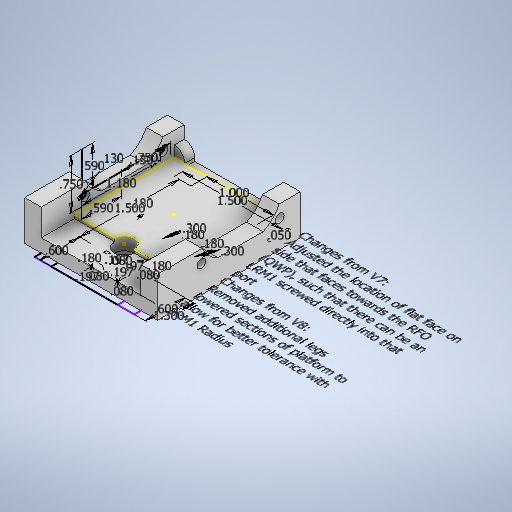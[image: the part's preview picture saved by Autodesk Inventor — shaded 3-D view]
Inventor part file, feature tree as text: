
AUTODESK INVENTOR PART (.ipt)
format: ipt  version: 2025.2 (Build 292293000, 293)  size: 535,040 bytes
history: native  units: in
note: dims shown in document units (in); Inventor stores cm internally (conversion verified against a paired STEP export)
features: sketch x15, extrude x13, thicken_offset x6, move_body x5, direct_edit x4, projected_geometry x2
ambient origin geometry x8: Origin, YZ Plane, XZ Plane, XY Plane, X Axis, Y Axis, Z Axis, Center Point
bodies: Solid1 (feature_tree)
feature tree (45):
  sketch  "Sketch1"  dims[d0=1.5in d1=1.0in]
  extrude  "Extrusion1"  Depth=1.5in
  extrude  "Extrusion2"  Depth=0.6in
  extrude  "Extrusion3"  Depth=1.5in
  extrude  "Extrusion4"  Depth=0.18in
  sketch  "Sketch3"  dims[d4=1.5in d5=0.18in]
  extrude  "Extrusion5"  Depth=0.05in
  sketch  "Sketch4"  dims[d6=0.18in d7=0.18in]
  extrude  "Extrusion6"  Depth=0.6in
  extrude  "Extrusion7"  Depth=0.3in
  extrude  "Extrusion8"  Depth=0.2in TaperAngle=0.0deg
  extrude  "Extrusion9"  Depth=0.2in TaperAngle=0.0deg
  thicken_offset  "Thicken1"
  thicken_offset  "Thicken2"
  thicken_offset  "Thicken3"
  thicken_offset  "Thicken4"
  thicken_offset  "Thicken5"
  thicken_offset  "Thicken6"
  extrude  "Extrusion10"  Depth=0.197in
  sketch  "Sketch10"  dims[d22=0.197in d23=0.197in]
  direct_edit  "Direct Edit1"
  sketch  "Sketch11"  dims[d24=0.08in d25=0.08in]
  extrude  "Extrusion11"  Depth=0.08in
  direct_edit  "Direct Edit2"
  extrude  "Extrusion12"  Depth=0.175in
  extrude  "Extrusion13"  Depth=0.4in
  direct_edit  "Direct Edit3"
  direct_edit  "Direct Edit4"
  sketch  "Sketch15"  dims[d33=1.0in d34=0.0in d35=0.05in d36=0.05in d37=1.55in d38=0.6in d39=0.0in d40=0.75in d41=0.59in d42=0.75in d43=0.59in d44=0.13in d45=1.18in d46=0.13in d47=2.0in d48=0.0in d49=0.25in d50=0.25in d51=2.0in d52=0.0in d53=0.2in d54=0.1in d55=0.2in d56=0.2in d57=0.3in d58=0.2in d59=0.3in d60=0.2in d61=0.1in d62=0.1in d63=0.2in d64=0.2in d66=1.75in d67=0.0in d68=0.0in d69=0.0in d70=-0.05in d71=0.0in d72=0.0in d73=-0.05in d74=0.197in d75=0.197in d76=0.08in d77=0.08in d78=0.16in d79=0.16in d80=0.16in d81=0.16in d82=0.16in d83=0.0in d84=0.0in d85=0.0in d86=-0.25in d87=0.24in d88=0.15in d89=0.5in d90=0.24in d91=0.5in d92=2.0in d93=0.0in d94=0.05in d95=0.0in d96=0.0in d97=0.0in d98=-0.01in d99=0.0in d100=0.0in d101=0.01in]
  sketch  "Sketch2"  dims[d2=0.18in d3=0.6in]
  sketch  "Sketch5"  dims[d8=0.25in d9=0.0in d10=0.05in]
  sketch  "Sketch6"  dims[d11=0.5in d12=0.0in d13=0.6in]
  sketch  "Sketch7"  dims[d14=0.3in d15=0.3in]
  sketch  "Sketch8"  dims[d16=0.3in d17=0.2in d18=0.0in]
  sketch  "Sketch9"  dims[d19=0.3in d20=0.2in d21=0.0in]
  sketch  "Sketch12"  dims[d26=0.175in d27=0.0in d28=0.18in]
  sketch  "Sketch13"  dims[d30=0.4in d31=0.4in]
  sketch  "Sketch14"  dims[d32=0.25in]
  projected_geometry  "Projected Loop1"
  projected_geometry  "Projected Loop2"
  move_body  "Move1"
  move_body  "Move2"
  move_body  "Move3"
  move_body  "Move4"
  move_body  "Move5"
